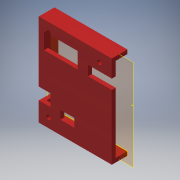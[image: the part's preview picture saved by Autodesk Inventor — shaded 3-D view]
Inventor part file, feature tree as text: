
AUTODESK INVENTOR PART (.ipt)
format: ipt  version: 2017 (Build 210142000, 142)  size: 242,688 bytes
history: native  units: in
note: dims shown in document units (in); Inventor stores cm internally (conversion verified against a paired STEP export)
features: reference x24, sketch x4, other x4, extrude x3, plane x1
ambient origin geometry x8: Origin, YZ Plane, XZ Plane, XY Plane, X Axis, Y Axis, Z Axis, Center Point
bodies: Solid1 (feature_tree)
feature tree (36):
  plane  "Work Plane1"
  extrude  "Extrusion1"  Depth=0.1in TaperAngle=0.0deg
  extrude  "Extrusion2"  Depth=0.03in
  extrude  "Extrusion3"  Depth=0.03in
  sketch  "Sketch4"  dims[d7=0.03in d8=0.03in d9=0.03in d10=0.03in d11=0.03in d12=0.03in d13=0.03in d14=0.03in d15=0.03in d16=0.03in d17=0.115in d18=0.115in d19=0.115in d20=0.1in d21=0.0in d22=0.1in d23=0.1in d24=0.1in d25=0.1in d26=0.3in d27=0.0in]
  sketch  "Sketch1"  dims[d0=0.05in d1=0.1in d2=0.0in]
  reference  "Reference1"
  sketch  "Sketch2"  dims[d3=0.03in d4=0.03in]
  reference  "Reference2"
  reference  "Reference3"
  reference  "Reference4"
  reference  "Reference5"
  reference  "Reference6"
  reference  "Reference7"
  reference  "Reference8"
  reference  "Reference9"
  reference  "Reference10"
  reference  "Reference11"
  reference  "Reference12"
  reference  "Reference13"
  reference  "Reference14"
  reference  "Reference15"
  reference  "Reference16"
  reference  "Reference17"
  reference  "Reference18"
  reference  "Reference19"
  reference  "Reference20"
  reference  "Reference21"
  reference  "Reference22"
  reference  "Reference23"
  reference  "Reference24"
  sketch  "Sketch3"  dims[d5=0.03in d6=0.03in]
  other  "<userpath>\Documents\Inventor\PixyCam and Gimbal\Assembly2.iam"
  other  "Assembly2.iam"
  other  "PixyCamKinda:1"
  other  "Assembly1"
